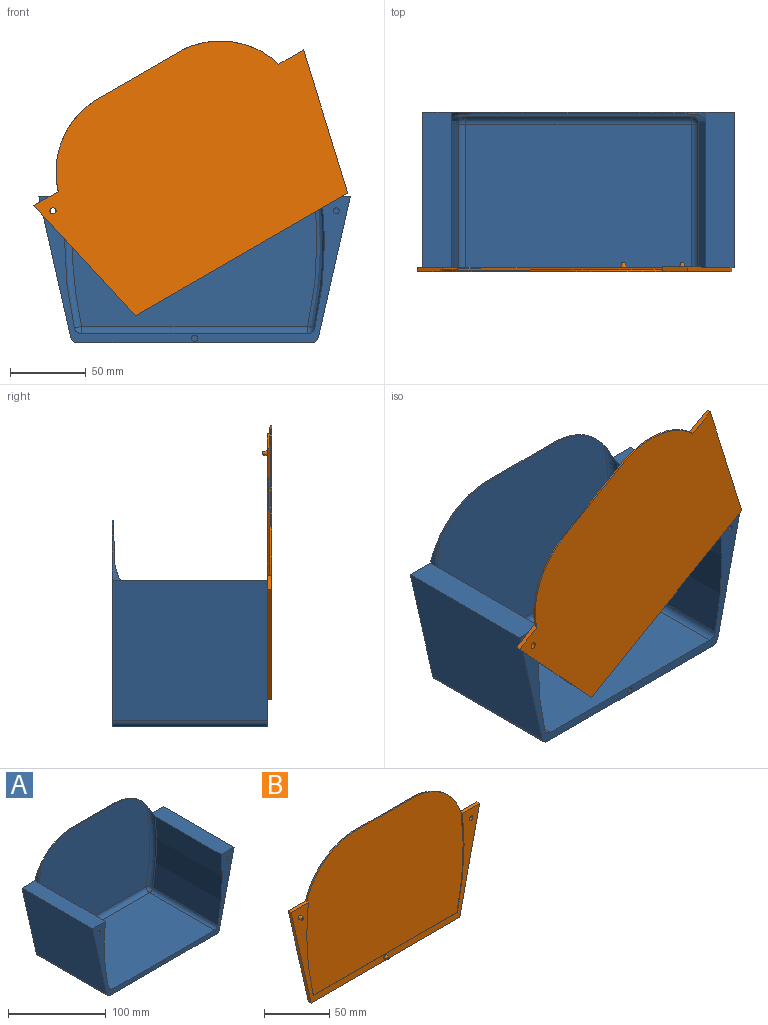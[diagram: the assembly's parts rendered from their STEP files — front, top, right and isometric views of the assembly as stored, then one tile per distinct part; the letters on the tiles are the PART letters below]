
ASSEMBLY  parts=2 mates=1
PART A: 28 faces, bbox 205.1x102.1x141.2 mm
  f0: cylinder r=2mm len=8.2mm, axis (0,1,0), area 103mm2, adj f16,f27
  f1: cylinder r=2mm len=8.2mm, axis (0,1,0), area 103mm2, adj f16,f26
  f2: plane 102x92.29mm, normal (-0.98,0,-0.22), area 9651.8mm2, adj f5,f11,f16,f24
  f3: plane 153.46x102mm, normal (0,0,-1), area 15653.3mm2, adj f11,f16,f24,f25
  f4: plane 102x92.29mm, normal (0.98,0,-0.22), area 9651.8mm2, adj f6,f11,f16,f25
  f5: plane 102x18.68mm, normal (0,0,1), area 1905.6mm2, adj f2,f9,f11,f14,f16
  f6: plane 102x18.68mm, normal (0,0,1), area 1905.6mm2, adj f4,f8,f11,f12,f16
  f7: cylinder r=2mm len=102mm, axis (0,1,0), area 1281.8mm2, adj f11,f16
  f8: cylinder r=255.55mm len=95.46mm, axis (0,1,0), area 8240.4mm2, adj f6,f16,f20,f23
  f9: cylinder r=255.55mm len=95.46mm, axis (0,1,0), area 8240.4mm2, adj f5,f16,f17,f18
  f10: plane 148.64x94.33mm, normal (0,0,1), area 14021.8mm2, adj f16,f17,f20,f21
  f11: plane 205x136mm, normal (0,1,0), area 23151mm2, adj f2,f3,f4,f5,f6,f7,f12,f13
  f12: cylinder r=56.3mm len=50.33mm, axis (0,1,0), area 106.8mm2, adj f6,f11,f13,f15,f23
  f13: plane 66.98x1mm, normal (0,0,1), area 67mm2, adj f11,f12,f14,f15
  f14: cylinder r=56.3mm len=50.33mm, axis (0,1,0), area 106.8mm2, adj f5,f11,f13,f15,f18
  f15: plane 161.23x125.2mm, normal (0,-1,0.01), area 18927.3mm2, adj f12,f13,f14,f18,f21,f23
  f16: plane 205x96.19mm, normal (0,-1,0), area 2481.4mm2, adj f0,f1,f2,f3,f4,f5,f6,f7
  f17: cylinder r=5mm len=94.33mm, axis (0,1,0), area 635.5mm2, adj f9,f10,f16,f19
  f18: bspline ~126.91x14.95mm, area 741.2mm2, adj f9,f14,f15,f19
  f19: sphere r=5mm, area 59.5mm2, adj f17,f18,f21
  f20: cylinder r=5mm len=94.33mm, axis (0,1,0), area 635.5mm2, adj f8,f10,f16,f22
  f21: cylinder r=5mm len=148.64mm, axis (-1,0,0), area 1157.5mm2, adj f10,f15,f19,f22
  f22: sphere r=5mm, area 20.8mm2, adj f20,f21,f23
  f23: bspline ~126.91x14.95mm, area 741.2mm2, adj f8,f12,f15,f22
  f24: cylinder r=5mm len=102mm, axis (0,-1,0), area 687.6mm2, adj f2,f3,f11,f16
  f25: cylinder r=5mm len=102mm, axis (0,1,0), area 687.6mm2, adj f3,f4,f11,f16
  f26: plane 4x4mm, normal (0,-1,0), area 12.6mm2, adj f1
  f27: plane 4x4mm, normal (0,-1,0), area 12.6mm2, adj f0
PART B: 19 faces, bbox 205x6x136 mm
  f0: plane 96.19x21.77mm, normal (-0.98,0,-0.22), area 295.9mm2, adj f1,f6,f9,f14
  f1: plane 161.45x3mm, normal (0,0,-1), area 484.4mm2, adj f0,f2,f9,f14
  f2: plane 96.19x21.77mm, normal (0.98,0,-0.22), area 295.9mm2, adj f1,f7,f9,f14
  f3: cylinder r=255.55mm len=90.19mm, axis (0,1,0), area 78.8mm2, adj f5,f7,f13,f14
  f4: cylinder r=255.55mm len=90.19mm, axis (0,1,0), area 78.8mm2, adj f5,f6,f13,f14
  f5: plane 156.56x0.27mm, normal (0,0,1), area 41.7mm2, adj f3,f4,f13,f14
  f6: plane 18.68x3mm, normal (0,0,1), area 56mm2, adj f0,f4,f9,f12,f14
  f7: plane 18.68x3mm, normal (0,0,1), area 56mm2, adj f2,f3,f9,f10,f14
  f8: cylinder r=2mm len=4mm, axis (0,1,0), area 37.7mm2, adj f9,f14
  f9: plane 205x136mm, normal (0,1,0), area 23157.2mm2, adj f0,f1,f2,f6,f7,f8,f10,f11
  f10: cylinder r=56.3mm len=50.33mm, axis (0,1,0), area 81.7mm2, adj f7,f9,f11,f13
  f11: plane 66.98x1mm, normal (0,0,1), area 67mm2, adj f9,f10,f12,f13
  f12: cylinder r=56.3mm len=50.33mm, axis (0,1,0), area 81.7mm2, adj f6,f9,f11,f13
  f13: plane 171.1x130.01mm, normal (0,-1,0.01), area 20652.5mm2, adj f3,f4,f5,f10,f11,f12
  f14: plane 205x96.19mm, normal (0,-1,0), area 2487.4mm2, adj f0,f1,f2,f3,f4,f5,f6,f7
  f15: plane 2x2mm, normal (0,-1,0), area 3.1mm2, adj f17
  f16: plane 2x2mm, normal (0,-1,0), area 3.1mm2, adj f18
  f17: cone r=2mm half-angle=14deg, axis (0,1,0), area 26.7mm2, adj f14,f15
  f18: cone r=2mm half-angle=14deg, axis (0,1,0), area 26.7mm2, adj f14,f16
PLACE A t=(-113.09,139.09,141.52)mm
PLACE B rot(axis=(0.26,0,-0.97),180deg) t=(126.92,34.09,317.38)mm
MATE revolute B.f8 <-> A.f7  axis (0,1,0) through (-157.42,37.09,65.91)mm
